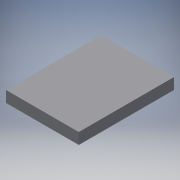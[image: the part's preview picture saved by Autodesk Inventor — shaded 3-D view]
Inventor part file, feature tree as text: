
AUTODESK INVENTOR PART (.ipt)
format: ipt  version: 2018 (Build 220112000, 112)  size: 189,952 bytes
history: native  units: mm
features: reference x5, extrude x4, sketch x4, plane x3, other x3, fillet x2, mirror x1
ambient origin geometry x8: Origin, YZ Plane, XZ Plane, XY Plane, X Axis, Y Axis, Z Axis, Center Point
bodies: Solid1 (feature_tree)
feature tree (22):
  extrude  "Extrusion1"  Depth=3.0mm
  extrude  "Extrusion2"  Depth=2.0mm TaperAngle=0.0deg
  sketch  "Sketch3"  dims[d5=5.0mm d6=5.0mm]
  plane  "Work Plane1"
  extrude  "Extrusion3"  Depth=5.0mm
  extrude  "Extrusion4"  Depth=2.0mm TaperAngle=0.0deg
  plane  "Work Plane2"
  mirror  "Mirror1"
  fillet  "Fillet1"  Radius=2.9mm
  fillet  "Fillet2"  Radius=2.9mm
  sketch  "Sketch1"  dims[d0=3.0mm d1=3.0mm]
  reference  "Reference1"
  reference  "Reference2"
  reference  "Reference3"
  reference  "Reference4"
  sketch  "Sketch2"  dims[d2=3.0mm d3=2.0mm d4=0.0mm]
  sketch  "Sketch4"  dims[d7=4.0mm d8=2.0mm d9=0.0mm d10=2.9mm d11=2.9mm d12=2.9mm d13=2.0mm d14=0.0mm d15=0.3mm d16=0.3mm d17=1.3mm d18=0.0mm d19=2.0mm d20=2.0mm]
  reference  "Reference5"
  plane  "Work Plane3"
  other  "<userpath>\Dropbox\Skola\Projekt\Kretsn_Brillz_V2\3D\Programmer_mini\Programmer_mini.iam"
  other  "Programmer_mini.iam"
  other  "Top:1"
